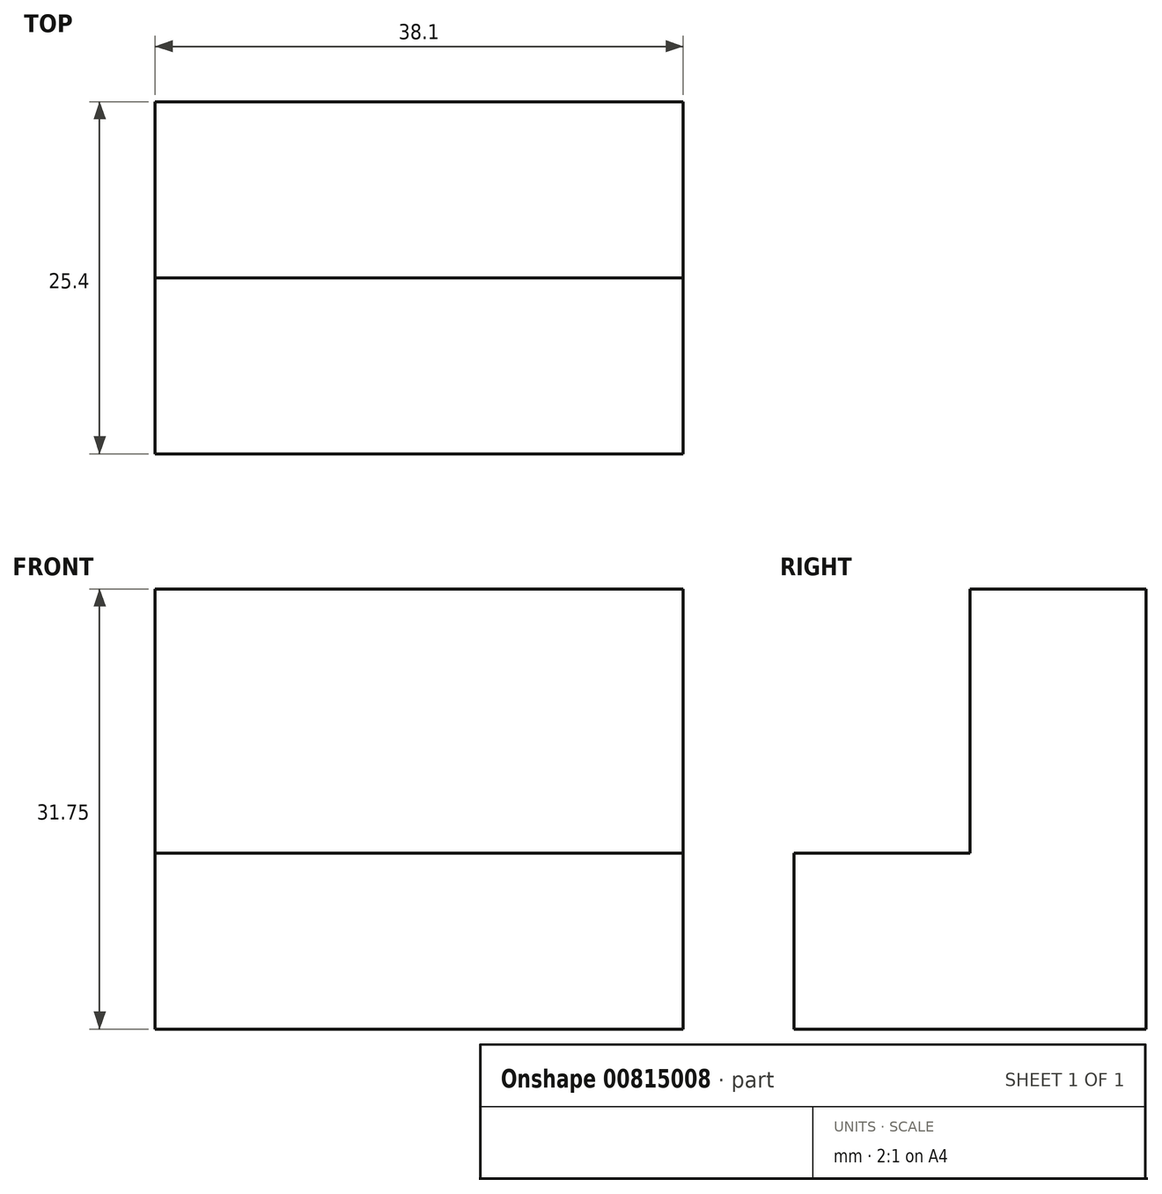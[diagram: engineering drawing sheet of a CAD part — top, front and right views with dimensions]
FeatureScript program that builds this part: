
annotation { "Feature Type Name" : "Feature", "Feature Type Description" : "" }
export const myFeature = defineFeature(function(context is Context, id is Id, definition is map)
    precondition{}
    {
        {
            var Q0;
            Q0=qCreatedBy(makeId("Right.planeOp"),FACE);
            var sketch = newSketch(context, id + "F0", { "sketchPlane" : qUnion([Q0])});
            skLineSegment(sketch, "E0", {"start": v(0, 0) * mm, "end": v(-25.4, 0) * mm});
            skLineSegment(sketch, "E1", {"start": v(-25.4, 0) * mm, "end": v(-25.4, 12.7) * mm});
            skLineSegment(sketch, "E2", {"start": v(-25.4, 12.7) * mm, "end": v(-12.7, 12.7) * mm});
            skPoint(sketch, "E2.endSnap0", {"position": v(-12.7, 0) * mm});
            skLineSegment(sketch, "E3", {"start": v(-12.7, 12.7) * mm, "end": v(-12.7, 31.75) * mm});
            skLineSegment(sketch, "E4", {"start": v(-12.7, 31.75) * mm, "end": v(0, 31.75) * mm});
            skLineSegment(sketch, "E5", {"start": v(0, 31.75) * mm, "end": v(0, 0) * mm});
            skSolve(sketch);
        }
        {
            var Q0;
            Q0=makeQuery(id+"F0.imprint","IMPRINT",FACE,{"disambiguationData":[TD([[makeQuery(id+"F0.imprint","IMPRINT",EDGE,{"derivedFrom":sQuery(id+"F0.wireOp",EDGE,"E0")}),-1.0]])]});
            extrude(context, id + "F1", {"entities" : qUnion([Q0]), "depth" : 38.1 * mm, "offsetDistance" : 25.4 * mm});
        }
    });
